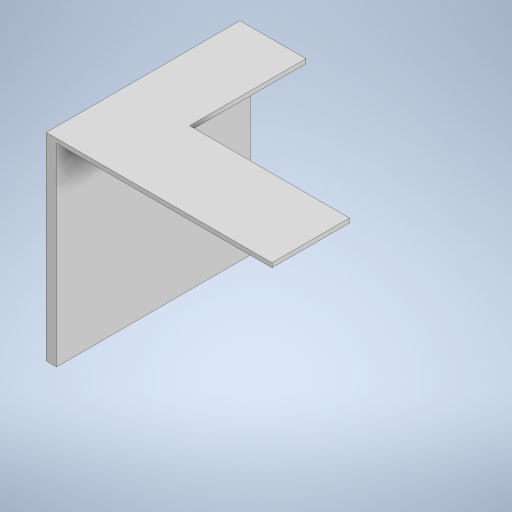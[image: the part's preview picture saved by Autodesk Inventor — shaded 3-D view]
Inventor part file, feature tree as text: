
AUTODESK INVENTOR PART (.ipt)
format: ipt  version: 2024 (Build 280153000, 153)  size: 325,632 bytes
history: native  units: mm
features: extrude x11, sketch x11
ambient origin geometry x8: Origin, YZ Plane, XZ Plane, XY Plane, X Axis, Y Axis, Z Axis, Center Point
bodies: Solid1 (feature_tree)
feature tree (22):
  extrude  "Top"  Depth=160.0mm
  extrude  "Right"  Depth=179.5mm
  extrude  "Left"  Depth=215.9mm
  extrude  "Plexiglass Cut"  Depth=25.4mm
  extrude  "Bottom"  Depth=50.8mm TaperAngle=0.0deg
  extrude  "Top Flattening"  Depth=50.8mm TaperAngle=0.0deg
  extrude  "Outer Side Flattening"  Depth=304.8mm TaperAngle=0.0deg
  extrude  "Bottom Flattening"  Depth=22.4mm TaperAngle=0.0deg
  extrude  "Inner Flattening"  Depth=22.389425mm
  extrude  "Bottom Cut"  Depth=22.4mm TaperAngle=0.0deg
  extrude  "Quarter Cut"  Depth=22.4mm TaperAngle=0.0deg
  sketch  "Sketch1"  dims[d11=220.0mm d12=160.0mm]
  sketch  "Sketch3"  dims[d15=248.6mm d16=179.5mm]
  sketch  "Sketch4"  dims[d18=304.8mm d19=215.9mm]
  sketch  "Sketch5"  dims[d20=25.4mm d21=0.0mm d22=25.4mm]
  sketch  "Sketch6"  dims[d25=266.7mm d26=50.8mm d27=0.0mm]
  sketch  "Sketch9"  dims[d28=266.7mm d29=50.8mm d30=0.0mm]
  sketch  "Sketch10"  dims[d31=12.7mm d32=304.8mm d33=0.0mm]
  sketch  "Sketch11"  dims[d34=25.4mm d35=0.0mm d46=22.4mm d47=0.0mm]
  sketch  "Sketch12"  dims[d48=22.389425mm d49=22.389425mm]
  sketch  "Sketch13"  dims[d50=0.0mm d51=0.0mm d52=22.4mm d53=0.0mm]
  sketch  "Sketch14"  dims[d54=296.8mm d55=22.4mm d56=0.0mm d57=0.0mm d58=0.0mm d59=0.0mm d60=0.0mm]
